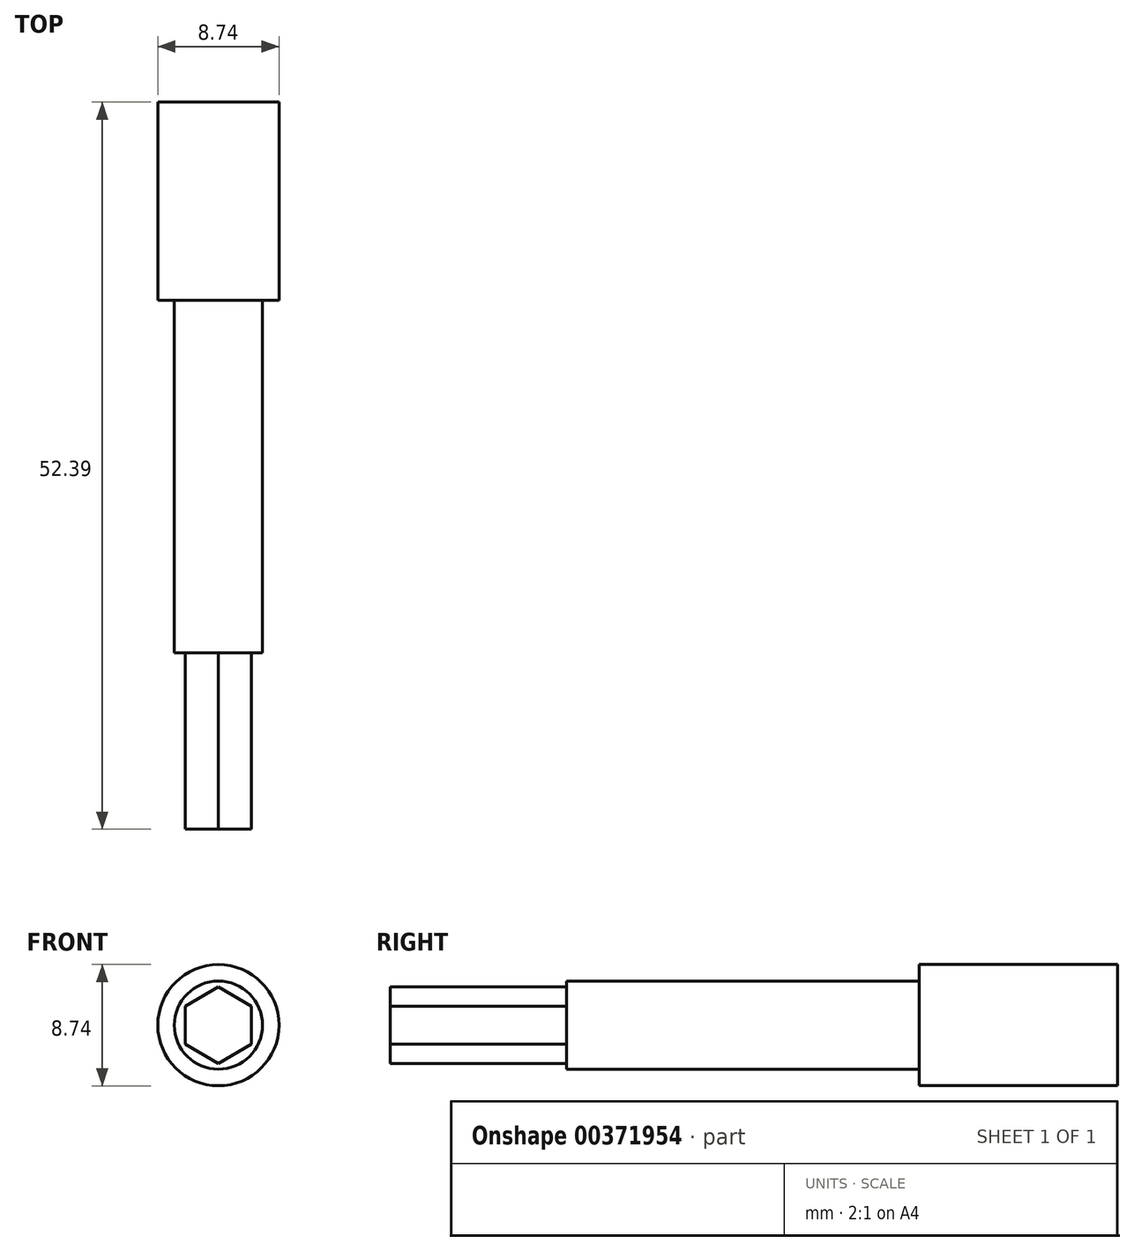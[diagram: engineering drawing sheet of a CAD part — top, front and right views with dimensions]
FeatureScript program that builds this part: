
annotation { "Feature Type Name" : "Feature", "Feature Type Description" : "" }
export const myFeature = defineFeature(function(context is Context, id is Id, definition is map)
    precondition{}
    {
        {
            var Q0;
            Q0=qCreatedBy(makeId("Front.planeOp"),FACE);
            var sketch = newSketch(context, id + "F0", { "sketchPlane" : qUnion([Q0])});
            skCircle(sketch, "E0", {"center": v(0, 0) * mm, "radius": 4.37 * mm});
            skSolve(sketch);
        }
        {
            var Q0;
            Q0 = qSketchRegion(id + "F0", true);
            extrude(context, id + "F1", {"entities" : qUnion([Q0]), "depth" : 14.29 * mm});
        }
        {
            var Q0;
            Q0=makeQuery(id+"F1.opExtrude","CAP_FACE",FACE,{"disambiguationData":[OSD([sQuery(id+"F0.wireOp",EDGE,"E0")])],"isStart":false});
            var sketch = newSketch(context, id + "F2", { "sketchPlane" : qUnion([Q0])});
            skCircle(sketch, "E1", {"center": v(0, 0) * mm, "radius": 3.18 * mm});
            skSolve(sketch);
        }
        {
            var Q0;
            Q0 = qSketchRegion(id + "F2", true);
            extrude(context, id + "F3", {"entities" : qUnion([Q0]), "operationType" : NewBodyOperationType.ADD, "depth" : 38.1 * mm});
        }
        {
            var Q0;
            Q0=makeQuery(id+"F3.opExtrude","CAP_FACE",FACE,{"disambiguationData":[OSD([sQuery(id+"F2.wireOp",EDGE,"E1")])],"isStart":false});
            var sketch = newSketch(context, id + "F4", { "sketchPlane" : qUnion([Q0])});
            skCircle(sketch, "E2.cCircle", {"center": v(0, 0) * mm, "radius": 2.38 * mm, "construction": true});
            skLineSegment(sketch, "E2.0", {"start": v(-2.38, -1.37) * mm, "end": v(-2.38, 1.37) * mm});
            skLineSegment(sketch, "E2.1", {"start": v(-2.38, 1.37) * mm, "end": v(0, 2.75) * mm});
            skLineSegment(sketch, "E2.2", {"start": v(0, 2.75) * mm, "end": v(2.38, 1.37) * mm});
            skLineSegment(sketch, "E2.3", {"start": v(2.38, 1.37) * mm, "end": v(2.38, -1.37) * mm});
            skLineSegment(sketch, "E2.4", {"start": v(2.38, -1.37) * mm, "end": v(0, -2.75) * mm});
            skLineSegment(sketch, "E2.5", {"start": v(0, -2.75) * mm, "end": v(-2.38, -1.37) * mm});
            skPoint(sketch, "E2.0.midPoint", {"position": v(-2.38, 0) * mm});
            skSolve(sketch);
        }
        {
            var Q0;
            Q0=makeQuery(id+"F4.imprint","IMPRINT",FACE,{"disambiguationData":[TD([[makeQuery(id+"F4.imprint","IMPRINT",EDGE,{"derivedFrom":sQuery(id+"F4.wireOp",EDGE,"E2.0")}),1.0]])]});
            extrude(context, id + "F5", {"entities" : qUnion([Q0]), "operationType" : NewBodyOperationType.REMOVE, "oppositeDirection" : true, "depth" : 12.7 * mm});
        }
    });
